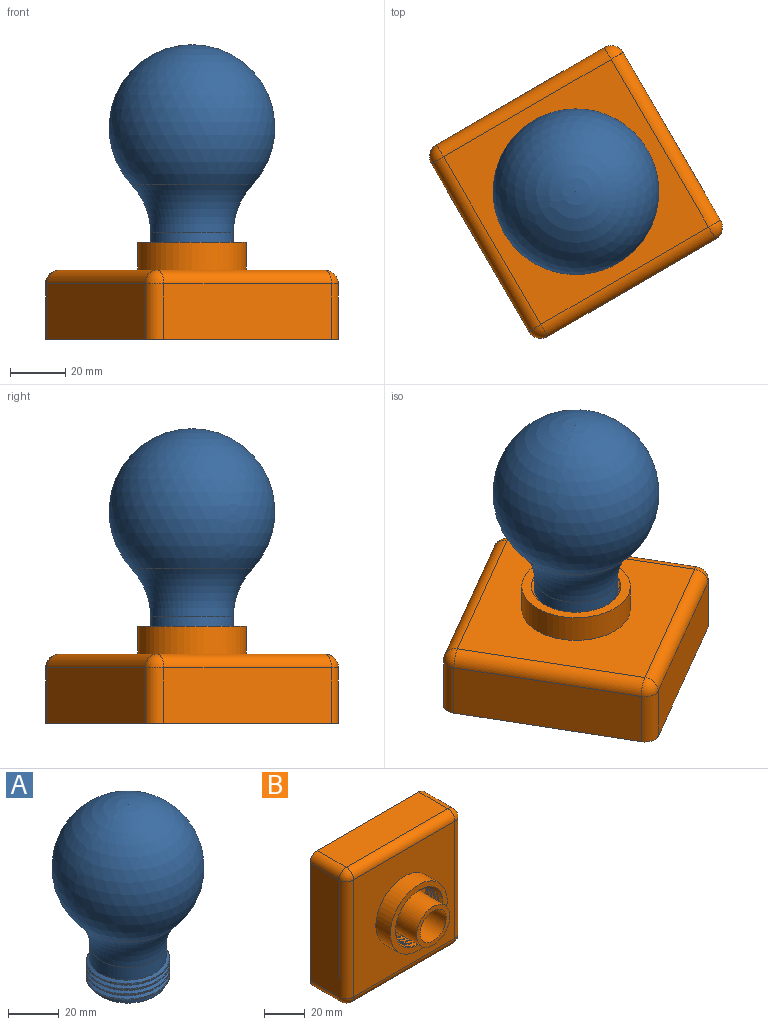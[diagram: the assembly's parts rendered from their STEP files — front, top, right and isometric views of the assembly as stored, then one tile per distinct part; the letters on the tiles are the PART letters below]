
ASSEMBLY  parts=2 mates=1
PART A: 16 faces, bbox 60x60x85 mm
  f0: cylinder r=12.5mm len=25mm, axis (0,0,-1), area 1354.9mm2, adj f1,f3
  f1: torus R=40mm, axis (0,0,-1), area 1967mm2, adj f0,f2
  f2: sphere r=27.5mm, area 8013mm2, adj f1
  f3: plane 30x30mm, normal (0,0,-1), area 216mm2, adj f0,f7,f8
  f4: sphere r=30mm, area 9536.1mm2, adj f5
  f5: torus R=40mm, axis (0,0,-1), area 2057.7mm2, adj f4,f6
  f6: cylinder r=15mm len=30mm, axis (0,0,-1), area 636.3mm2, adj f5,f10,f12,f13,f14
  f7: cylinder r=15mm len=30mm, axis (0,0,-1), area 29.5mm2, adj f3,f8,f14
  f8: cylinder r=15mm len=30mm, axis (0,0,-1), area 111.9mm2, adj f3,f7,f9,f11,f13,f14
  f9: cylinder r=15mm len=30mm, axis (0,0,-1), area 47.1mm2, adj f8,f10,f13,f14
  f10: cylinder r=15mm len=30mm, axis (0,0,-1), area 47.1mm2, adj f6,f9,f13,f14
  f11: plane 2.02x1.46mm, normal (0,-1,0), area 1.7mm2, adj f8,f13,f14,f15
  f12: plane 2.02x1.46mm, normal (0,1,0), area 1.7mm2, adj f6,f13,f14,f15
  f13: bspline ~38.64x33.46mm, area 582.5mm2, adj f6,f8,f9,f10,f11,f12,f15
  f14: bspline ~38.64x33.46mm, area 582mm2, adj f6,f7,f8,f9,f10,f11,f12,f15
  f15: bspline ~33.48x33.48mm, area 258.8mm2, adj f11,f12,f13,f14
PART B: 55 faces, bbox 80.4x45.4x80.4 mm
  f0: plane 58.46x22.5mm, normal (0,0,-1), area 1315.4mm2, adj f1,f7,f28,f39
  f1: plane 75x75mm, normal (0,1,0), area 5111.7mm2, adj f0,f2,f3,f4,f15,f22,f23,f24
  f2: plane 58.46x22.5mm, normal (1,0,0), area 1315.4mm2, adj f1,f7,f34,f38
  f3: plane 58.46x22.5mm, normal (0,0,1), area 1315.4mm2, adj f1,f7,f24,f33
  f4: plane 58.46x22.5mm, normal (-1,0,0), area 1315.4mm2, adj f1,f7,f23,f29
  f5: cylinder r=15.1mm len=30.2mm, axis (0,1,0), area 180mm2, adj f6,f18,f19,f21,f42
  f6: plane 30.27x30.22mm, normal (0,-1,0), area 301mm2, adj f5,f13,f19,f42
  f7: plane 80x80mm, normal (0,1,0), area 962.1mm2, adj f0,f2,f3,f4,f8,f9,f10,f11
  f8: plane 70x20mm, normal (0,0,1), area 1400mm2, adj f7,f43,f48,f50
  f9: plane 70x20mm, normal (-1,0,0), area 1400mm2, adj f7,f44,f48,f52
  f10: plane 70x20mm, normal (0,0,-1), area 1400mm2, adj f7,f46,f52,f54
  f11: plane 70x20mm, normal (1,0,0), area 1400mm2, adj f7,f45,f50,f54
  f12: plane 70x70mm, normal (0,-1,0), area 3693.1mm2, adj f16,f43,f44,f45,f46
  f13: cylinder r=11.5mm len=23mm, axis (0,1,0), area 1445.1mm2, adj f6,f14
  f14: plane 23x23mm, normal (0,-1,0), area 161mm2, adj f13,f15
  f15: cylinder r=9mm len=22.5mm, axis (0,1,0), area 1272.3mm2, adj f1,f14
  f16: cylinder r=19.6mm len=39.2mm, axis (0,1,0), area 1231.5mm2, adj f12,f17
  f17: plane 39.59x39.59mm, normal (0,-1,0), area 379.8mm2, adj f16,f18,f20,f21
  f18: cone r=15.1mm half-angle=45deg, axis (0,-1,0), area 59.8mm2, adj f5,f17,f20,f21,f42
  f19: plane 2x1.73mm, normal (0,0,-1), area 1.7mm2, adj f5,f6,f20,f21,f42
  f20: bspline ~38.87x33.66mm, area 678.2mm2, adj f17,f18,f19,f21,f42
  f21: bspline ~38.87x33.66mm, area 660.6mm2, adj f5,f17,f18,f19,f20
  f22: cylinder r=4.13mm len=22.5mm, axis (0,-1,0), area 146.1mm2, adj f1,f7,f23,f24
  f23: plane 22.5x4.13mm, normal (0,0,1), area 93mm2, adj f1,f4,f7,f22
  f24: plane 22.5x4.13mm, normal (-1,0,0), area 93mm2, adj f1,f3,f7,f22
  f25: cylinder r=2mm len=12mm, axis (0,1,0), area 150.8mm2, adj f7,f26
  f26: cone r=0mm half-angle=59deg, axis (0,1,0), area 14.7mm2, adj f25
  f27: cylinder r=4.13mm len=22.5mm, axis (0,-1,0), area 146.1mm2, adj f1,f7,f28,f29
  f28: plane 22.5x4.13mm, normal (-1,0,0), area 93mm2, adj f0,f1,f7,f27
  f29: plane 22.5x4.13mm, normal (0,0,-1), area 93mm2, adj f1,f4,f7,f27
  f30: cylinder r=2mm len=12mm, axis (0,1,0), area 150.8mm2, adj f7,f31
  f31: cone r=0mm half-angle=59deg, axis (0,1,0), area 14.7mm2, adj f30
  f32: cylinder r=4.13mm len=22.5mm, axis (0,-1,0), area 146.1mm2, adj f1,f7,f33,f34
  f33: plane 22.5x4.13mm, normal (1,0,0), area 93mm2, adj f1,f3,f7,f32
  f34: plane 22.5x4.13mm, normal (0,0,1), area 93mm2, adj f1,f2,f7,f32
  f35: cylinder r=2mm len=12mm, axis (0,1,0), area 150.8mm2, adj f7,f36
  f36: cone r=0mm half-angle=59deg, axis (0,1,0), area 14.7mm2, adj f35
  f37: cylinder r=4.13mm len=22.5mm, axis (0,-1,0), area 146.1mm2, adj f1,f7,f38,f39
  f38: plane 22.5x4.13mm, normal (0,0,-1), area 93mm2, adj f1,f2,f7,f37
  f39: plane 22.5x4.13mm, normal (1,0,0), area 93mm2, adj f0,f1,f7,f37
  f40: cylinder r=2mm len=12mm, axis (0,1,0), area 150.8mm2, adj f7,f41
  f41: cone r=0mm half-angle=59deg, axis (0,1,0), area 14.7mm2, adj f40
  f42: bspline ~30.51x30.51mm, area 111.9mm2, adj f5,f6,f18,f19,f20
  f43: cylinder r=5mm len=70mm, axis (1,0,0), area 549.8mm2, adj f8,f12,f47,f49
  f44: cylinder r=5mm len=70mm, axis (0,0,1), area 549.8mm2, adj f9,f12,f47,f51
  f45: cylinder r=5mm len=70mm, axis (0,0,-1), area 549.8mm2, adj f11,f12,f49,f53
  f46: cylinder r=5mm len=70mm, axis (-1,0,0), area 549.8mm2, adj f10,f12,f51,f53
  f47: sphere r=5mm, area 39.3mm2, adj f43,f44,f48
  f48: cylinder r=5mm len=20mm, axis (0,1,0), area 157.1mm2, adj f7,f8,f9,f47
  f49: sphere r=5mm, area 39.3mm2, adj f43,f45,f50
  f50: cylinder r=5mm len=20mm, axis (0,-1,0), area 157.1mm2, adj f7,f8,f11,f49
  f51: sphere r=5mm, area 39.3mm2, adj f44,f46,f52
  f52: cylinder r=5mm len=20mm, axis (0,-1,0), area 157.1mm2, adj f7,f9,f10,f51
  f53: sphere r=5mm, area 39.3mm2, adj f45,f46,f54
  f54: cylinder r=5mm len=20mm, axis (0,1,0), area 157.1mm2, adj f7,f10,f11,f53
PLACE A rot(axis=(0,0,1),30.2deg) t=(-2.35,-188.6,46.59)mm
PLACE B rot(axis=(-0.93,-0.25,0.25),93.9deg) t=(-23.75,-247.3,-29.79)mm
MATE cylindrical A.f0 <-> B.f5  axis (0,0,-1) through (-2.35,-188.6,0.21)mm
